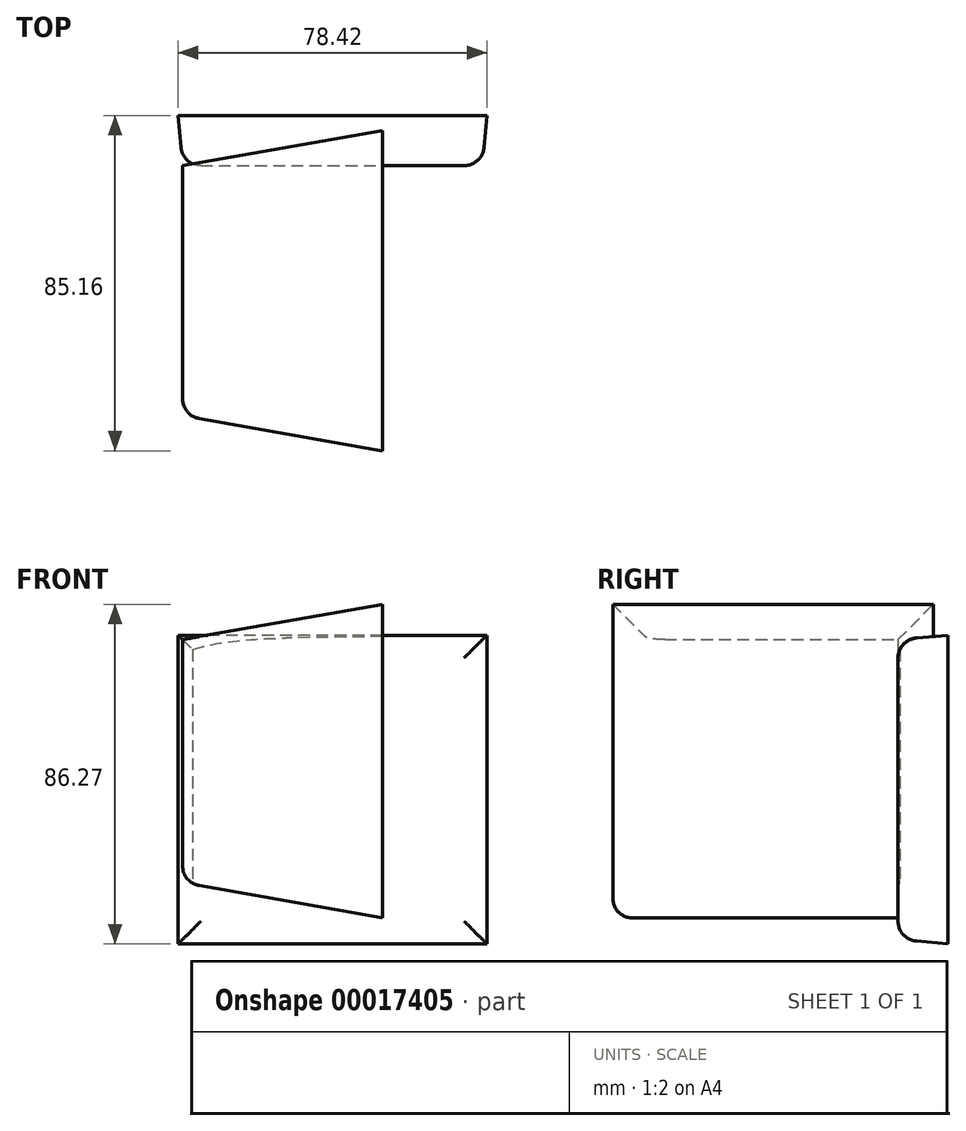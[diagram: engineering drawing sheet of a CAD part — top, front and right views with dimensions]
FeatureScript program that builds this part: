
annotation { "Feature Type Name" : "Feature", "Feature Type Description" : "" }
export const myFeature = defineFeature(function(context is Context, id is Id, definition is map)
    precondition{}
    {
        {
            var Q0;
            Q0=qCreatedBy(makeId("Front.planeOp"),FACE);
            var sketch = newSketch(context, id + "F0", { "sketchPlane" : qUnion([Q0])});
            skLineSegment(sketch, "E0.bottom", {"start": v(0, 0) * mm, "end": v(76.2, 0) * mm});
            skLineSegment(sketch, "E0.top", {"start": v(0, -76.2) * mm, "end": v(76.2, -76.2) * mm});
            skLineSegment(sketch, "E0.left", {"start": v(0, 0) * mm, "end": v(0, -76.2) * mm});
            skLineSegment(sketch, "E0.right", {"start": v(76.2, 0) * mm, "end": v(76.2, -76.2) * mm});
            skSolve(sketch);
        }
        {
            var Q0;
            Q0=makeQuery(id+"F0.imprint","IMPRINT",FACE,{"disambiguationData":[TD([[makeQuery(id+"F0.imprint","IMPRINT",EDGE,{"derivedFrom":sQuery(id+"F0.wireOp",EDGE,"E0.bottom")}),-1.0]])]});
            extrude(context, id + "F1", {"entities" : qUnion([Q0]), "oppositeDirection" : true, "depth" : 12.7 * mm, "hasDraft" : true, "draftAngle" : 5 * degree});
        }
        {
            var Q0;
            Q0=makeQuery(id+"F1.opExtrude","CAP_EDGE",EDGE,{"disambiguationData":[OSD([sQuery(id+"F0.wireOp",EDGE,"E0.bottom")])],"isStart":true});
            var Q1;
            Q1=makeQuery(id+"F1.opExtrude","CAP_FACE",FACE,{"disambiguationData":[OSD([sQuery(id+"F0.wireOp",EDGE,"E0.bottom"),sQuery(id+"F0.wireOp",EDGE,"E0.top"),sQuery(id+"F0.wireOp",EDGE,"E0.left"),sQuery(id+"F0.wireOp",EDGE,"E0.right")])],"isStart":true});
            fillet(context, id + "F2", {"entities" : qUnion([Q0, Q1]), "radius" : 5.08 * mm, "tangentPropagation" : true, "allowEdgeOverflow" : false});
        }
        {
            var Q0;
            Q0=qCreatedBy(makeId("Right.planeOp"),FACE);
            var sketch = newSketch(context, id + "F3", { "sketchPlane" : qUnion([Q0])});
            skLineSegment(sketch, "E1.bottom", {"start": v(0, 0) * mm, "end": v(-63.5, 0) * mm});
            skLineSegment(sketch, "E1.top", {"start": v(0, -61.74) * mm, "end": v(-63.5, -61.74) * mm});
            skLineSegment(sketch, "E1.left", {"start": v(0, 0) * mm, "end": v(0, -61.74) * mm});
            skLineSegment(sketch, "E1.right", {"start": v(-63.5, 0) * mm, "end": v(-63.5, -61.74) * mm});
            skSolve(sketch);
        }
        {
            var Q0;
            Q0 = qSketchRegion(id + "F3", true);
            extrude(context, id + "F4", {"entities" : qUnion([Q0]), "operationType" : NewBodyOperationType.ADD, "depth" : 50.8 * mm, "hasDraft" : true, "draftAngle" : 10 * degree});
        }
        {
            var Q0;
            Q0=makeQuery(id+"F4.opExtrude","SWEPT_EDGE",EDGE,{"disambiguationData":[OSD([sQuery(id+"F3.wireOp",EDGE,"E1.top"),sQuery(id+"F3.wireOp",EDGE,"E1.right")])]});
            var Q1;
            Q1=makeQuery(id+"F4.opExtrude","CAP_EDGE",EDGE,{"disambiguationData":[OSD([sQuery(id+"F3.wireOp",EDGE,"E1.top")])],"isStart":true});
            var Q2;
            Q2=makeQuery(id+"F4.opExtrude","CAP_EDGE",EDGE,{"disambiguationData":[OSD([sQuery(id+"F3.wireOp",EDGE,"E1.right")])],"isStart":true});
            fillet(context, id + "F5", {"entities" : qUnion([Q0, Q1, Q2]), "radius" : 5.08 * mm, "tangentPropagation" : true, "allowEdgeOverflow" : false});
        }
    });
